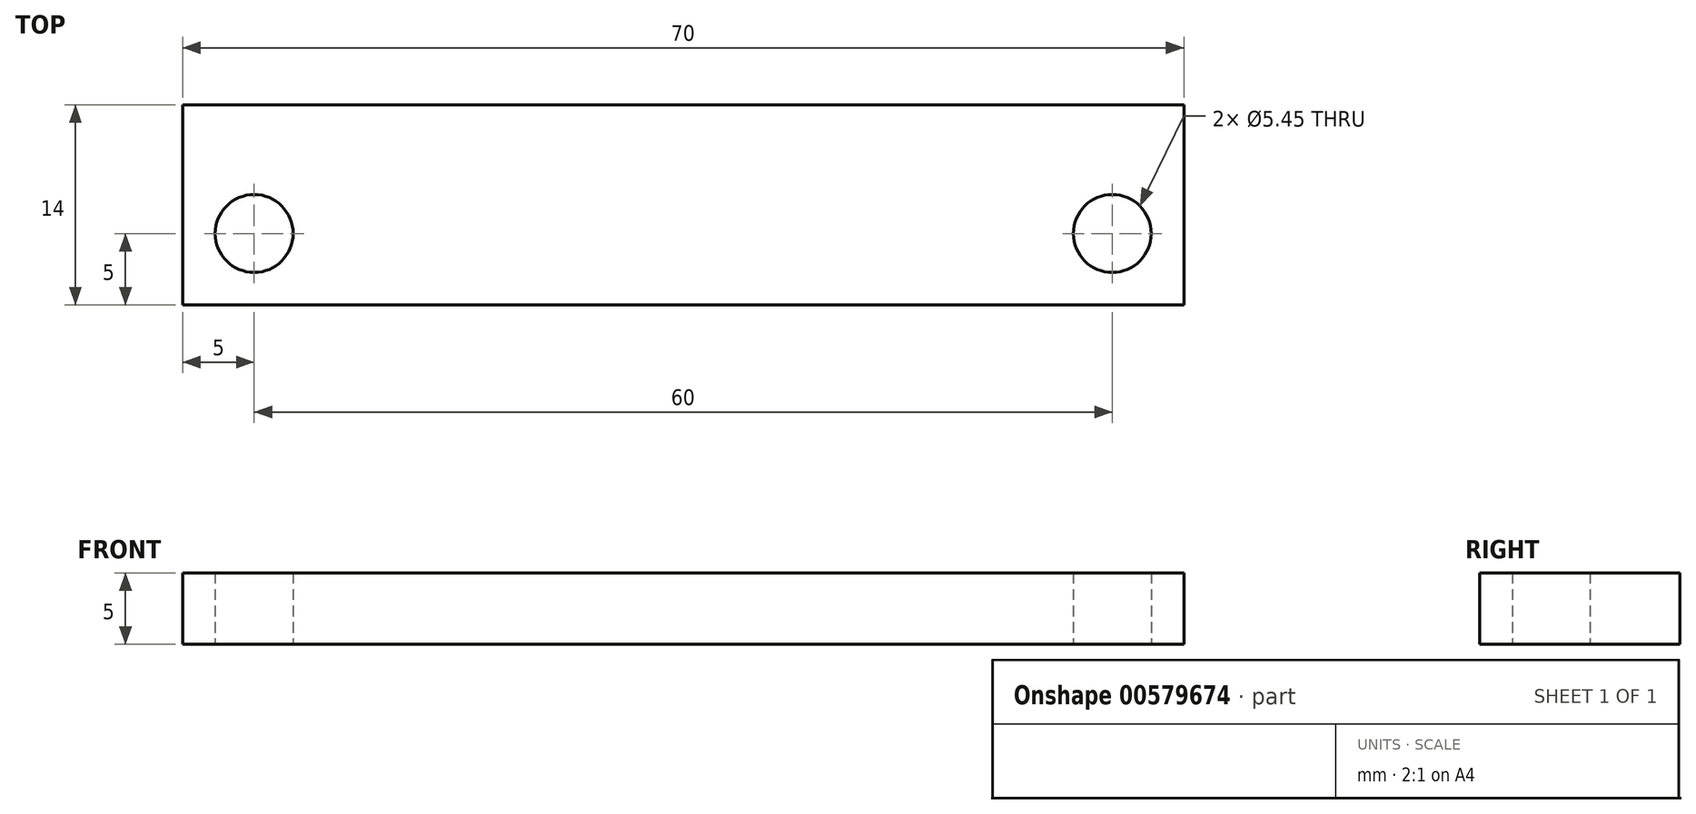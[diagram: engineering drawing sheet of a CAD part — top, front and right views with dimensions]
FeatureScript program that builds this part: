
annotation { "Feature Type Name" : "Feature", "Feature Type Description" : "" }
export const myFeature = defineFeature(function(context is Context, id is Id, definition is map)
    precondition{}
    {
        {
            var Q0;
            Q0=qCreatedBy(makeId("Top.planeOp"),FACE);
            var sketch = newSketch(context, id + "F0", { "sketchPlane" : qUnion([Q0])});
            skLineSegment(sketch, "E0.bottom", {"start": v(-35, 7) * mm, "end": v(35, 7) * mm});
            skLineSegment(sketch, "E0.top", {"start": v(-35, -7) * mm, "end": v(35, -7) * mm});
            skLineSegment(sketch, "E0.left", {"start": v(-35, 7) * mm, "end": v(-35, -7) * mm});
            skLineSegment(sketch, "E0.right", {"start": v(35, 7) * mm, "end": v(35, -7) * mm});
            skCircle(sketch, "E1", {"center": v(-30, -2) * mm, "radius": 2.73 * mm});
            skCircle(sketch, "E2.1.0.0", {"center": v(30, -2) * mm, "radius": 2.73 * mm});
            skLineSegment(sketch, "E2.direction1", {"start": v(-30, -2) * mm, "end": v(30, -2) * mm, "construction": true});
            skSolve(sketch);
        }
        {
            var Q0;
            Q0=makeQuery(id+"F0.imprint","IMPRINT",FACE,{"disambiguationData":[TD([[makeQuery(id+"F0.imprint","IMPRINT",EDGE,{"derivedFrom":sQuery(id+"F0.wireOp",EDGE,"E0.bottom")}),-1.0]])]});
            extrude(context, id + "F1", {"entities" : qUnion([Q0]), "depth" : 5 * mm, "offsetDistance" : 25 * mm});
        }
    });
